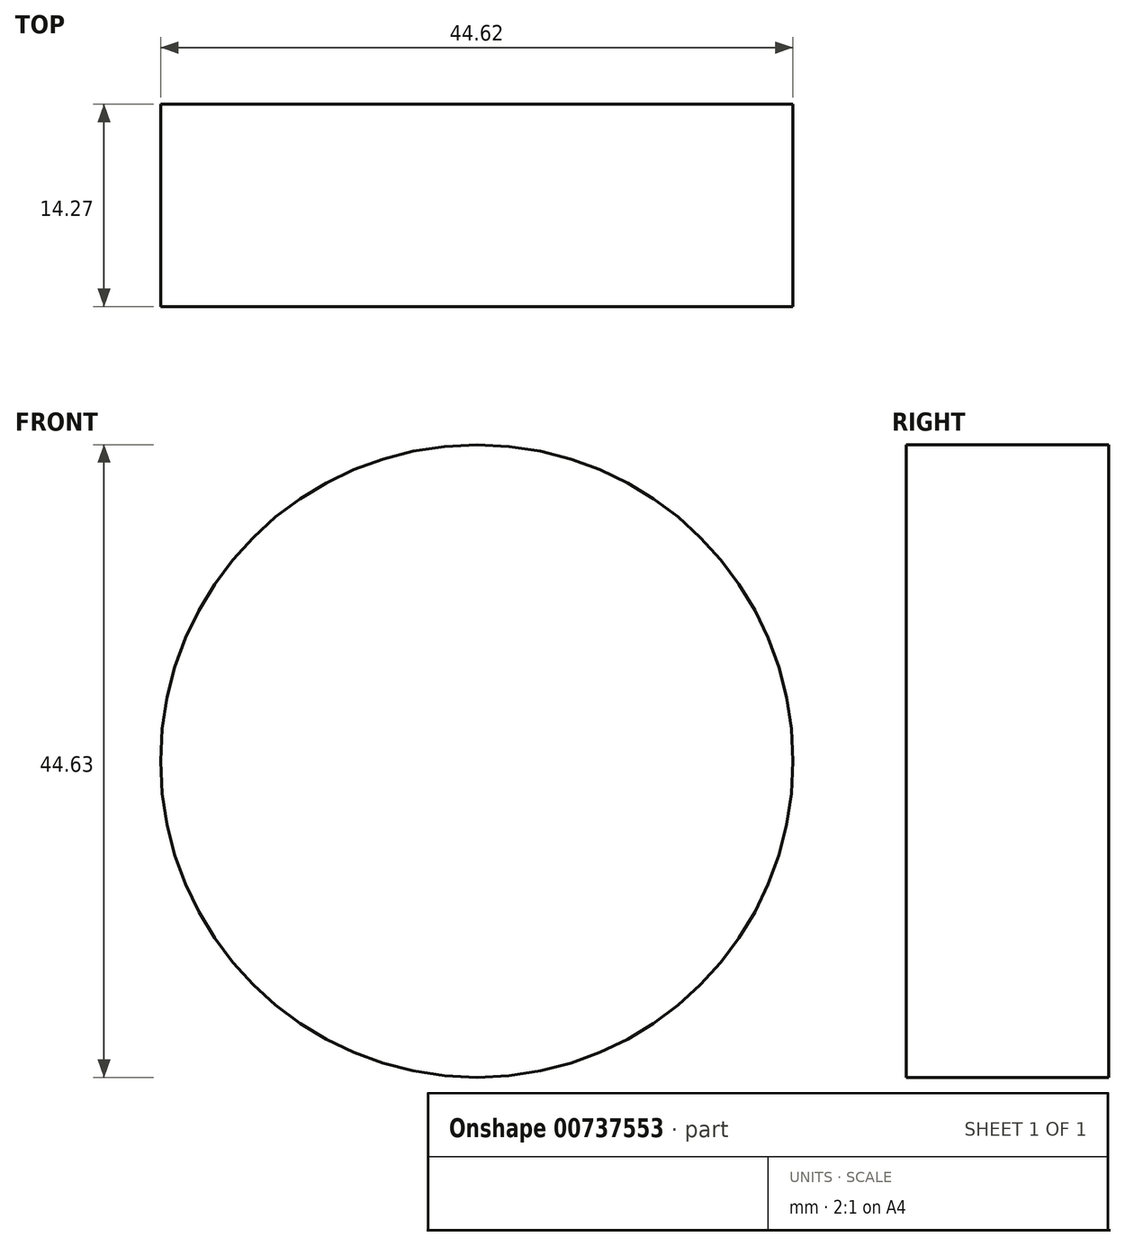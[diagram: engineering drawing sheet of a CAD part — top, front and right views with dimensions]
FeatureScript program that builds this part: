
annotation { "Feature Type Name" : "Feature", "Feature Type Description" : "" }
export const myFeature = defineFeature(function(context is Context, id is Id, definition is map)
    precondition{}
    {
        {
            var Q0;
            Q0=qCreatedBy(makeId("Front.planeOp"),FACE);
            var sketch = newSketch(context, id + "F0", { "sketchPlane" : qUnion([Q0])});
            skCircle(sketch, "E0", {"center": v(0, 22.31) * mm, "radius": 22.31 * mm});
            skSolve(sketch);
        }
        {
            var Q0;
            Q0 = qSketchRegion(id + "F0", true);
            extrude(context, id + "F1", {"entities" : qUnion([Q0]), "depth" : 14.27 * mm, "offsetDistance" : 25.4 * mm});
        }
    });
